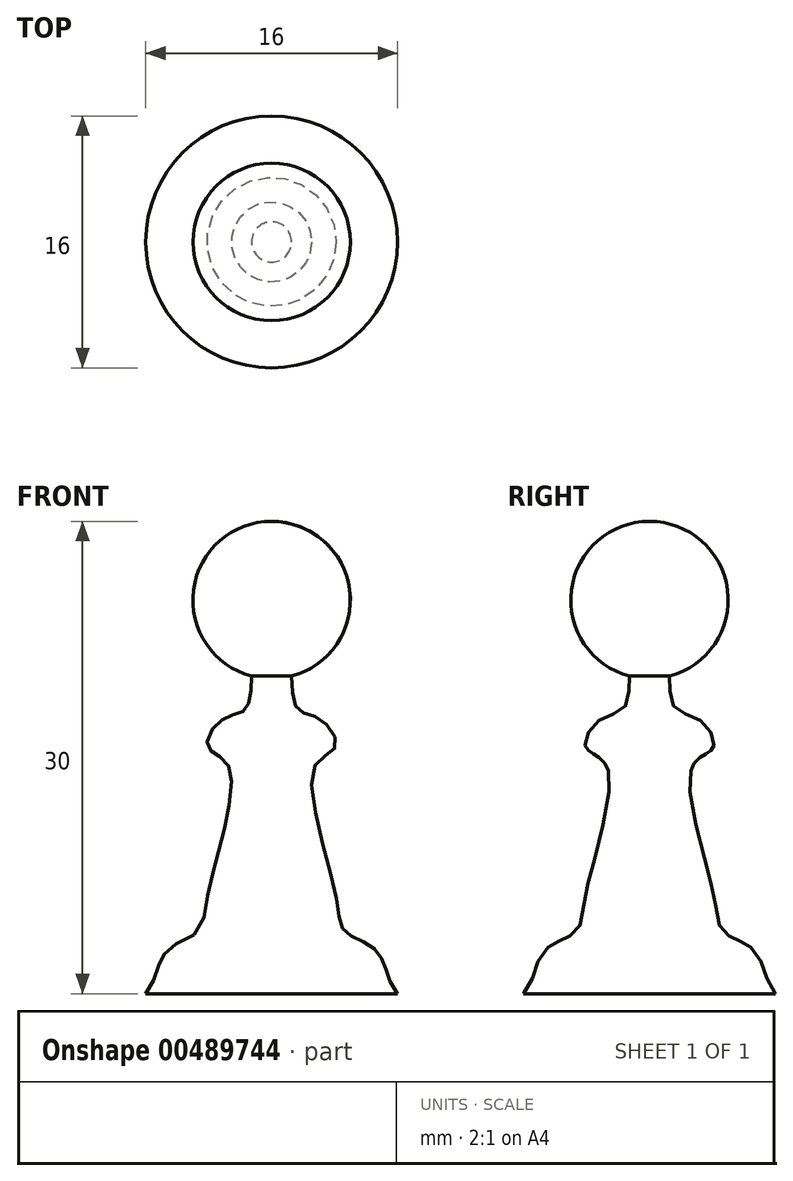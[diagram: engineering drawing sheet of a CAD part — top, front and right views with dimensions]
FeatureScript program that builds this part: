
annotation { "Feature Type Name" : "Feature", "Feature Type Description" : "" }
export const myFeature = defineFeature(function(context is Context, id is Id, definition is map)
    precondition{}
    {
        {
            var Q0;
            Q0=qCreatedBy(makeId("Front.planeOp"),FACE);
            var sketch = newSketch(context, id + "F0", { "sketchPlane" : qUnion([Q0])});
            skLineSegment(sketch, "E0.bottom", {"start": v(0, -12.6) * mm, "end": v(8, -12.6) * mm});
            skLineSegment(sketch, "E0.left", {"start": v(0, -12.6) * mm, "end": v(0, 7.4) * mm});
            skArc(sketch, "E1", {"start": v(1.27, 7.56) * mm, "mid": v(4.96, 13.03) * mm, "end": v(0, 17.4) * mm});
            skFitSpline(sketch, "E2", {"points": [v(8, -12.6) * mm, v(7.2, -10.83) * mm, v(6.33, -9.6) * mm, v(4.68, -8.67) * mm, v(4.06, -6.3) * mm, v(2.72, 1.83) * mm, v(4.06, 3.07) * mm, v(3.13, 4.82) * mm, v(1.7, 5.43) * mm, v(1.27, 7.56) * mm], "startDerivative": vector(-15.08, 17.17) * mm, "endDerivative": vector(-0.35, 24.76) * mm});
            skLineSegment(sketch, "E3", {"start": v(0, 7.4) * mm, "end": v(0, 17.4) * mm});
            skSolve(sketch);
        }
        {
            var Q0;
            Q0=qCreatedBy(makeId("Front.planeOp"),FACE);
            var sketch = newSketch(context, id + "F1", { "sketchPlane" : qUnion([Q0])});
            skLineSegment(sketch, "E4", {"start": v(0, 28.08) * mm, "end": v(0, -27.3) * mm});
            skSolve(sketch);
        }
        {
            var Q0;
            Q0=makeQuery(id+"F0.imprint","IMPRINT",FACE,{"disambiguationData":[TD([[makeQuery(id+"F0.imprint","IMPRINT",EDGE,{"derivedFrom":sQuery(id+"F0.wireOp",EDGE,"E0.bottom")}),1.0]])]});
            var Q1;
            Q1=sQuery(id+"F1.wireOp",EDGE,"E4");
            revolve(context, id + "F2", {"entities" : qUnion([Q0]), "axis" : qUnion([Q1]), "revolveType" : RevolveType.FULL});
        }
    });
